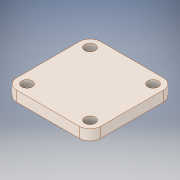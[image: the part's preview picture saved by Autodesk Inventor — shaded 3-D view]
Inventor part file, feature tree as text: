
AUTODESK INVENTOR PART (.ipt)
format: ipt  version: 2019 (Build 230136000, 136)  size: 123,392 bytes
history: mixed  units: in
note: dims shown in document units (in); Inventor stores cm internally (conversion verified against a paired STEP export)
features: extrude x1, sketch x1, other x1, imported_body x1
ambient origin geometry x8: Origin, YZ Plane, XZ Plane, XY Plane, X Axis, Y Axis, Z Axis, Center Point
bodies: Solid1 (imported_parasolid)
feature tree (4):
  extrude  "Extrusion1"  Depth=0.3937in
  sketch  "Sketch1"  dims[d0=0.2in d1=0.2in d2=0.2in d3=0.2in d4=0.3937in d5=0.0in]
  other  "Base-Flange1"
  imported_body  NMx_Import_Brep_tag  [imported B-rep: ~14 faces, bbox_mm=[40.0, 5.0, 40.0]]
